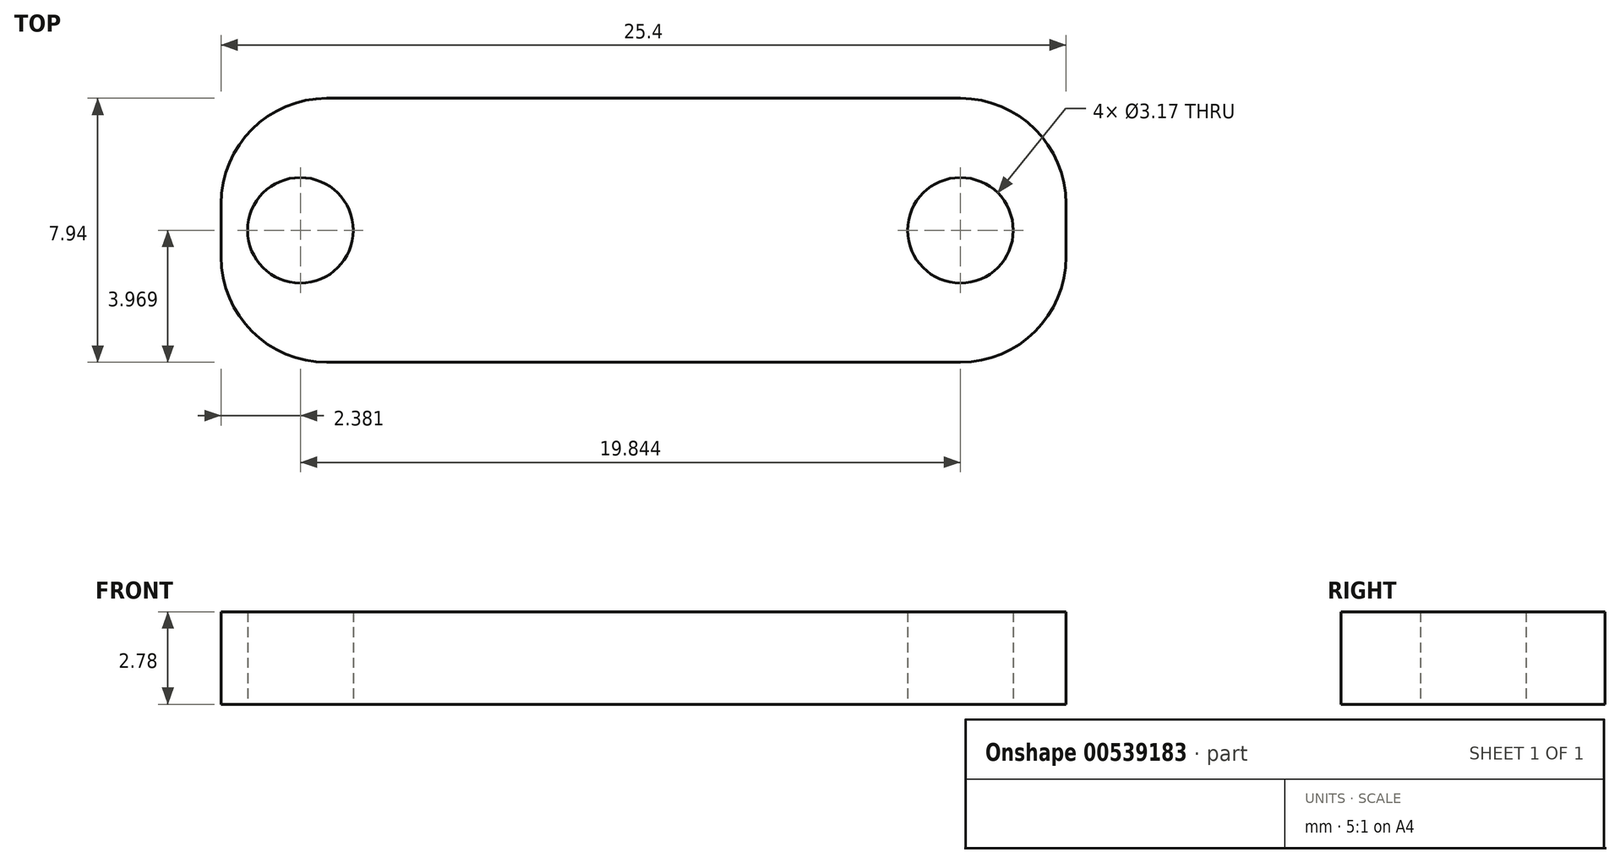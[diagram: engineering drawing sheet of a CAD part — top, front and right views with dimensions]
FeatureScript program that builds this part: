
annotation { "Feature Type Name" : "Feature", "Feature Type Description" : "" }
export const myFeature = defineFeature(function(context is Context, id is Id, definition is map)
    precondition{}
    {
        {
            var Q0;
            Q0=qCreatedBy(makeId("Top.planeOp"),FACE);
            var sketch = newSketch(context, id + "F0", { "sketchPlane" : qUnion([Q0])});
            skLineSegment(sketch, "E0.bottom", {"start": v(3.18, 0) * mm, "end": v(22.22, 0) * mm});
            skLineSegment(sketch, "E0.top", {"start": v(3.18, 7.94) * mm, "end": v(22.22, 7.94) * mm});
            skLineSegment(sketch, "E0.left", {"start": v(0, 3.18) * mm, "end": v(0, 4.76) * mm});
            skLineSegment(sketch, "E0.right", {"start": v(25.4, 3.18) * mm, "end": v(25.4, 4.76) * mm});
            skCircle(sketch, "E1", {"center": v(2.38, 3.97) * mm, "radius": 1.59 * mm});
            skLineSegment(sketch, "E2", {"start": v(12.7, 7.94) * mm, "end": v(12.7, 0) * mm});
            skPoint(sketch, "E3.visualSharp", {"position": v(0, 7.94) * mm});
            skArc(sketch, "E3.filletArc", {"start": v(3.18, 7.94) * mm, "mid": v(0.93, 7) * mm, "end": v(0, 4.76) * mm});
            skPoint(sketch, "E4.visualSharp", {"position": v(0, 0) * mm});
            skArc(sketch, "E4.filletArc", {"start": v(0, 3.18) * mm, "mid": v(0.93, 0.93) * mm, "end": v(3.18, 0) * mm});
            skArc(sketch, "E5.MirrorCS", {"start": v(22.22, 7.94) * mm, "mid": v(24.47, 7) * mm, "end": v(25.4, 4.76) * mm});
            skArc(sketch, "E6.MirrorCS", {"start": v(25.4, 3.18) * mm, "mid": v(24.47, 0.93) * mm, "end": v(22.22, 0) * mm});
            skPoint(sketch, "E7.orphan", {"position": v(25.4, 7.94) * mm});
            skPoint(sketch, "E8.orphan", {"position": v(25.4, 0) * mm});
            skCircle(sketch, "E9", {"center": v(22.23, 3.97) * mm, "radius": 1.59 * mm});
            skSolve(sketch);
        }
        {
            var Q0;
            Q0=makeQuery(id+"F0.imprint","IMPRINT",FACE,{"disambiguationData":[TD([[makeQuery(id+"F0.imprint","IMPRINT",EDGE,{"derivedFrom":sQuery(id+"F0.wireOp",EDGE,"E0.right")}),1.0]])]});
            var Q1;
            Q1=makeQuery(id+"F0.imprint","IMPRINT",FACE,{"disambiguationData":[TD([[makeQuery(id+"F0.imprint","IMPRINT",EDGE,{"derivedFrom":sQuery(id+"F0.wireOp",EDGE,"E0.left")}),-1.0]])]});
            extrude(context, id + "F1", {"entities" : qUnion([Q0, Q1]), "depth" : 2.78 * mm, "offsetDistance" : 25.4 * mm});
        }
    });
